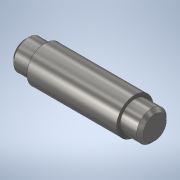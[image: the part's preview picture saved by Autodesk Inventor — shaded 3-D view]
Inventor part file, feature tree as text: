
AUTODESK INVENTOR PART (.ipt)
format: ipt  version: 2020 (Build 240168000, 168)  size: 202,240 bytes
history: native  units: mm
features: chamfer x2, revolve x1, sketch x1
ambient origin geometry x8: Origin, YZ Plane, XZ Plane, XY Plane, X Axis, Y Axis, Z Axis, Center Point
bodies: Solid1 (feature_tree)
feature tree (4):
  revolve  "Revolution1"  [1 undecoded]
  chamfer  "Chamfer1"  Distance=12.0mm
  chamfer  "Chamfer2"  Distance=2.0mm
  sketch  "Sketch1"  dims[d0=78.0mm d1=8.95mm d2=12.0mm d3=2.0mm d4=54.0mm d5=2.0mm d6=90.0deg d7=2.0mm d8=2.0mm d9=45.0deg d10=2.0mm d11=2.0mm d12=45.0deg]
note: 1 required parameter value undecoded (feature->parameter linkage not recoverable at this tier; creation-order binding heuristic only, values carry confidence <= 0.55)
